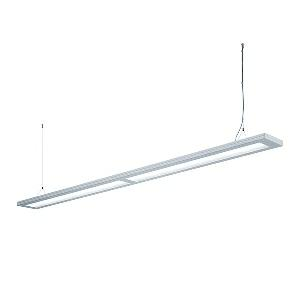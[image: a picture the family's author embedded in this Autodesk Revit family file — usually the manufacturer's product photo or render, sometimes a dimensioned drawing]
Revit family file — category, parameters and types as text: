
# Revit family: lavigo_-_dpp_24000_840_r_g2_00801387_0fdb
name_source: partatom
category: Lighting Fixtures
units: mm (PartAtom-declared; Revit-internal decimal feet)

## family parameters
Cut with Voids When Loaded = No
Host = Face
Light Source = No
Part Type = Normal
Room Calculation Point = No
Round Connector Dimension = Use Diameter
Shared = No

## types (1)
- LAVIGO - DPP 24000/840/R/G2 (1 x LED, 24000 lm, 4000K)
    Apparent Load = 158 VA
    Approval mark = CE
    CIE Flux Codes = 60 87 97 14 100
    Color Rendering = 80-89
    Color Temperature = 4000K
    Control Gear = Electronic ballast
    Default Elevation = 1800 mm
    Description = DPP 24000/840/R/G2|Suspended luminaire|light source: LED|connected load: 220-240 V, 50/60 Hz|Power consumption: approx. 158 W|standby: approx. 0,50|luminous flux: 24000 lm|luminous efficacy: 151 lm/W|light distribution: Direct/indirect|direct ratio: approx. 14 %|colour temperature: Cold white, ca. 4000 K|color rendering index (CRI): >= 80|chromaticity tolerance:  3 SDCM|System of protection: IP 20|technology: Presence and daylight sensor control (PIR)|luminaire body|material: Steel/plastic|surface: Powder coatet|colour: Silver metallic|lamp cover: Polycarbonate (PC), Clear|mains lead: 1.00 m With free stranded wires|Fastening: Steel cable 0.3 - 0.7 m|decorative contrast side parts: Flint grey|glare control: Prism aperture|luminance(L65): <= 2700 cd/m|unified glare rating(4H 8H): <=  16|special features: Canopy colour (pure white), Push button in luminaire head, Cradle to Cradle Certified TM, Direct light component with edge light and light-guide technology for homogenous light exit, Flicker-free, Integrated light and presence sensor PIR, Retrofittable with TALK module, Separated, direct and indirect light individually adjustable|
    Frequency = 50 Hz
    Height = 36 mm
    Lamp = 1 x LED
    Lamp Light Flux = 24000 lm
    Lamp count = 1
    Length = 2430 mm
    Luminous efficacy = 152 lm/W
    Manufacturer = Waldmann
    ModVariant = No
    Model = 00801387
    Mounting Place = Ceiling
    Mounting Type = Pendant
    Number of Poles = 1
    OnlyDefault = Yes
    Power Factor = 1
    Product Name = LAVIGO - DPP 24000/840/R/G2
    Product group = Suspended luminaire
    ProductGroupID = 9
    Protection Class = Protection class I
    Protection Degree = IP 20
    RLX_Detail_Level = 1
    RLX_Emergency_Light_Flux = 0 lm
    RLX_Emergency_Type = 0
    RLX_Emergency_Type_DB = No
    RlxData = <blob elided: 26461 chars, md5=11560860>
    Socket = socket
    Standby Power = 0 W
    System Light Flux = 24000 lm
    System Power = 158 W
    Type Comments = Product without accessories
    Type Image = 121742000-00681441.jpg
    URL = http://relux.com
    VarID = ---
    Voltage = 230 V
    Voltage Range = 220-240 V
    Weight = 0.00 kg
    Width = 200 mm  [stored 0.656168 ft]

note: [stored X ft] marks values corroborated as IEEE doubles in the binary element streams (Revit-internal decimal feet)

## geometry (parser evidence)
native form markers: Blend x4, Sweep x12
no freeform markers — native parametric forms only
